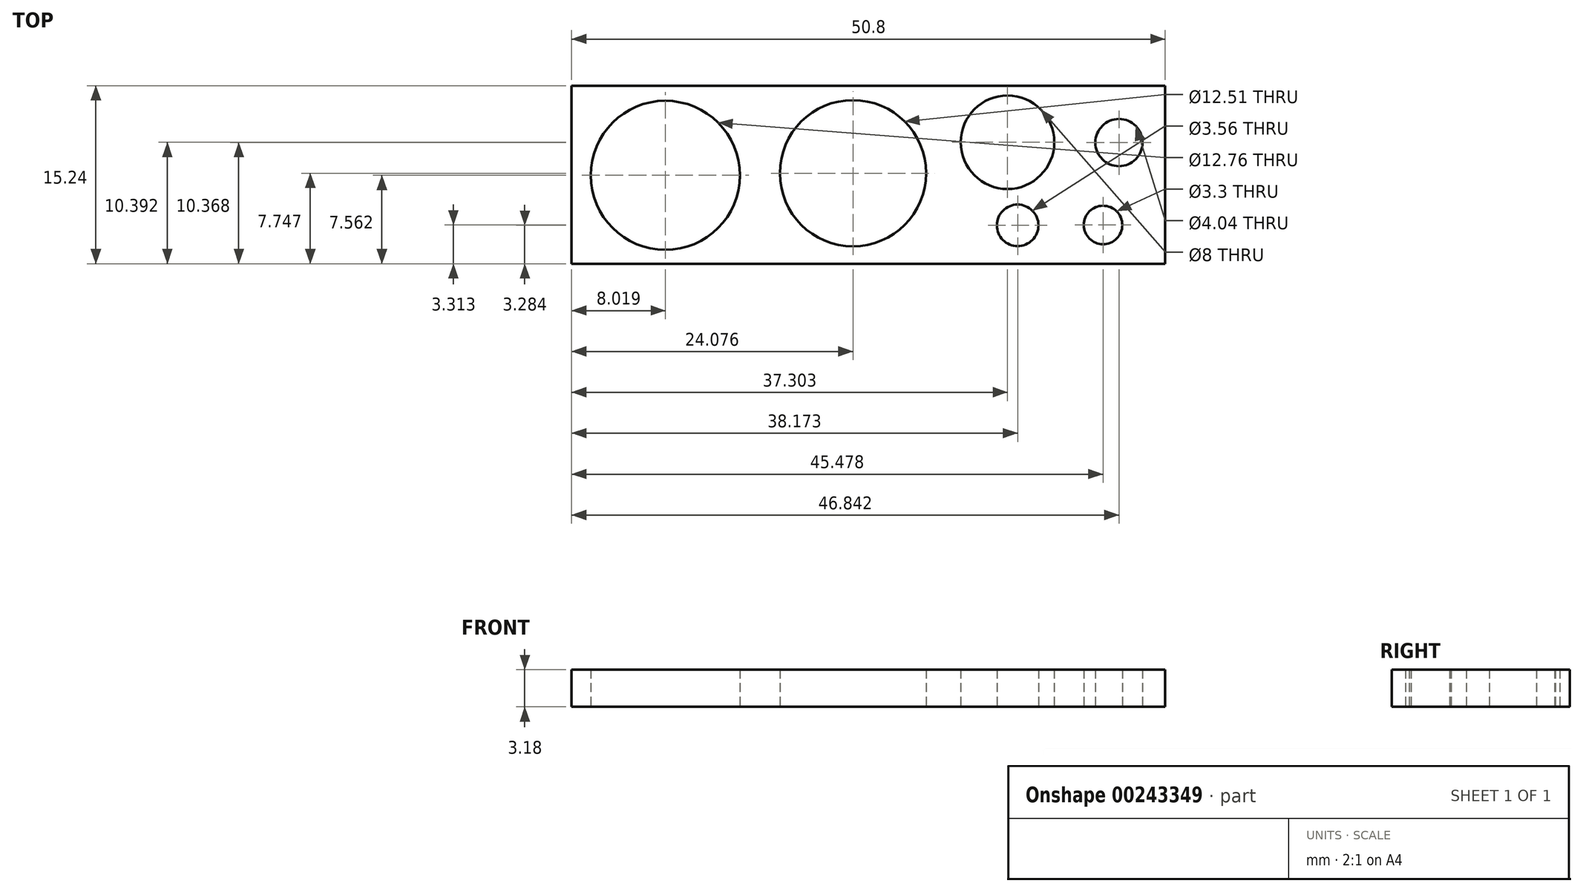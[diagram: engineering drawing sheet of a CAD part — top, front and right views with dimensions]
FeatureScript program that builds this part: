
annotation { "Feature Type Name" : "Feature", "Feature Type Description" : "" }
export const myFeature = defineFeature(function(context is Context, id is Id, definition is map)
    precondition{}
    {
        {
            var Q0;
            Q0=qCreatedBy(makeId("Top.planeOp"),FACE);
            var sketch = newSketch(context, id + "F0", { "sketchPlane" : qUnion([Q0])});
            skPoint(sketch, "E0.middle", {"position": v(0, 0) * mm});
            skCircle(sketch, "E1", {"center": v(-26.72, 7.75) * mm, "radius": 6.25 * mm});
            skCircle(sketch, "E2", {"center": v(-12.63, 3.28) * mm, "radius": 1.78 * mm});
            skCircle(sketch, "E3", {"center": v(-42.78, 7.56) * mm, "radius": 6.38 * mm});
            skCircle(sketch, "E4", {"center": v(-5.32, 3.31) * mm, "radius": 1.65 * mm});
            skCircle(sketch, "E5", {"center": v(-3.96, 10.37) * mm, "radius": 2.02 * mm});
            skCircle(sketch, "E6", {"center": v(-13.5, 10.4) * mm, "radius": 4 * mm});
            skLineSegment(sketch, "E7.bottom", {"start": v(-50.8, 15.24) * mm, "end": v(0, 15.24) * mm});
            skLineSegment(sketch, "E7.top", {"start": v(-50.8, 0) * mm, "end": v(0, 0) * mm});
            skLineSegment(sketch, "E7.left", {"start": v(-50.8, 15.24) * mm, "end": v(-50.8, 0) * mm});
            skLineSegment(sketch, "E7.right", {"start": v(0, 15.24) * mm, "end": v(0, 0) * mm});
            skSolve(sketch);
        }
        {
            var Q0;
            Q0 = qSketchRegion(id + "F0", true);
            extrude(context, id + "F1", {"entities" : qUnion([Q0]), "depth" : 3.17 * mm});
        }
    });
